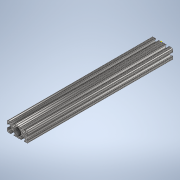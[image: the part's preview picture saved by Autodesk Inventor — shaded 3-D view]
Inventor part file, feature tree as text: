
AUTODESK INVENTOR PART (.ipt)
format: ipt  version: 2020 (Build 240168000, 168)  size: 347,648 bytes
history: native  units: in
note: dims shown in document units (in); Inventor stores cm internally (conversion verified against a paired STEP export)
features: sketch x2, extrude x1
ambient origin geometry x8: Origin, YZ Plane, XZ Plane, XY Plane, X Axis, Y Axis, Z Axis, Center Point
bodies: Solid1 (feature_tree)
feature tree (3):
  extrude  "Extrusion1"  [1 undecoded]
  sketch  "Sketch2"
  sketch  "Sketch1"  dims[d0=14.0in d1=0.0in]
note: 1 required parameter value undecoded (feature->parameter linkage not recoverable at this tier; creation-order binding heuristic only, values carry confidence <= 0.55)
